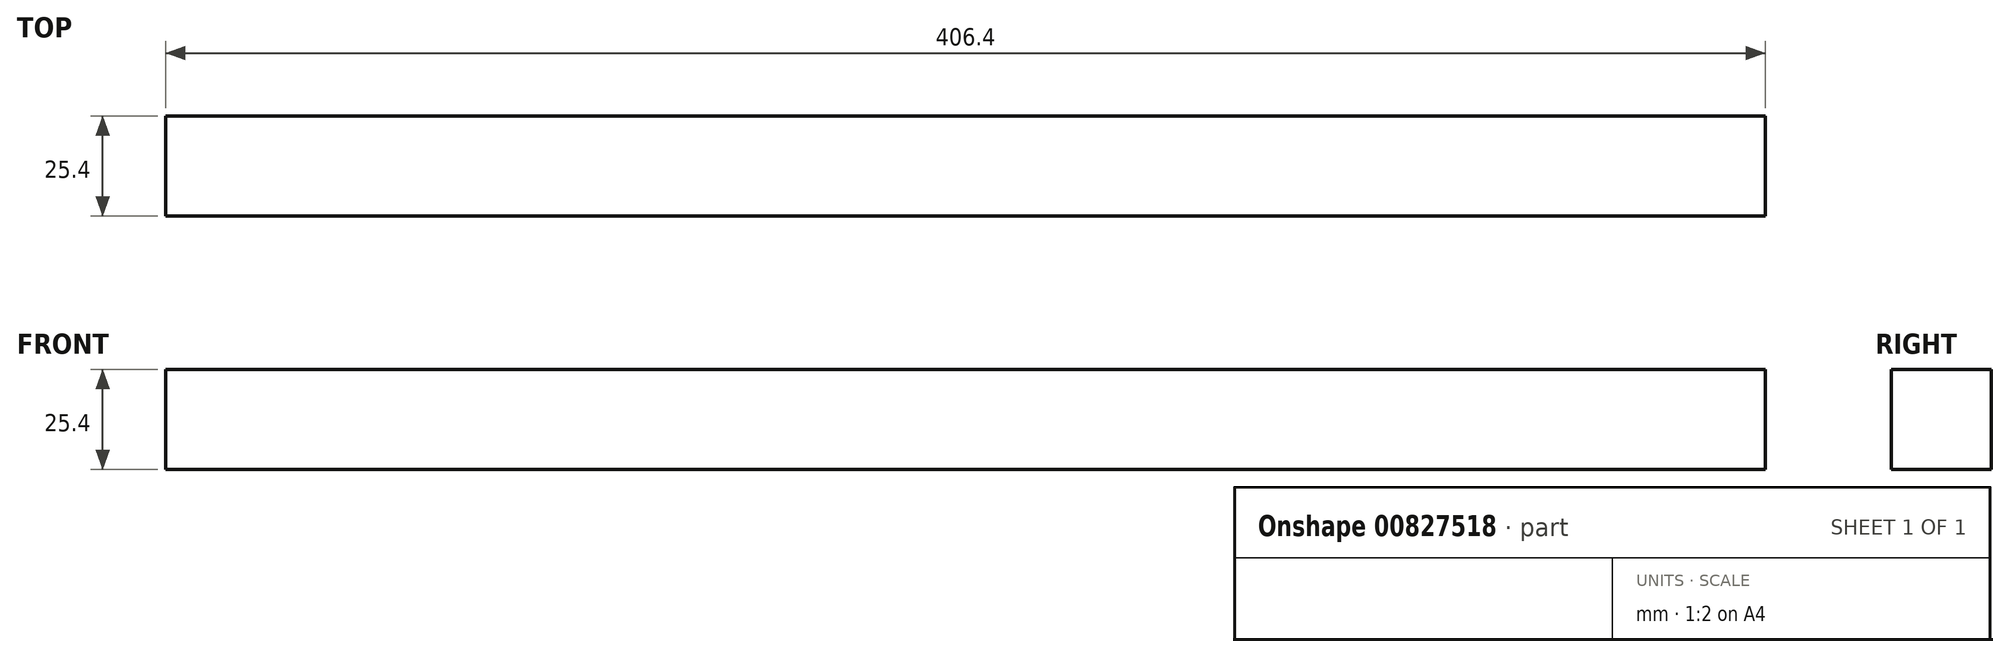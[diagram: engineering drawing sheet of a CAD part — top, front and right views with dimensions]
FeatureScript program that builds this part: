
annotation { "Feature Type Name" : "Feature", "Feature Type Description" : "" }
export const myFeature = defineFeature(function(context is Context, id is Id, definition is map)
    precondition{}
    {
        {
            var Q0;
            Q0=qCreatedBy(makeId("Front.planeOp"),FACE);
            var sketch = newSketch(context, id + "F0", { "sketchPlane" : qUnion([Q0])});
            skLineSegment(sketch, "E0", {"start": v(-203.2, 12.7) * mm, "end": v(203.2, 12.7) * mm});
            skLineSegment(sketch, "E1", {"start": v(203.2, 12.7) * mm, "end": v(203.2, -12.7) * mm});
            skLineSegment(sketch, "E2", {"start": v(203.2, -12.7) * mm, "end": v(-203.2, -12.7) * mm});
            skLineSegment(sketch, "E3", {"start": v(-203.2, 12.7) * mm, "end": v(-203.2, -12.7) * mm});
            skSolve(sketch);
        }
        {
            var Q0;
            Q0=makeQuery(id+"F0.imprint","IMPRINT",FACE,{"disambiguationData":[TD([[makeQuery(id+"F0.imprint","IMPRINT",EDGE,{"derivedFrom":sQuery(id+"F0.wireOp",EDGE,"E0")}),-1.0]])]});
            extrude(context, id + "F1", {"entities" : qUnion([Q0]), "depth" : 25.4 * mm, "offsetDistance" : 25.4 * mm});
        }
    });
